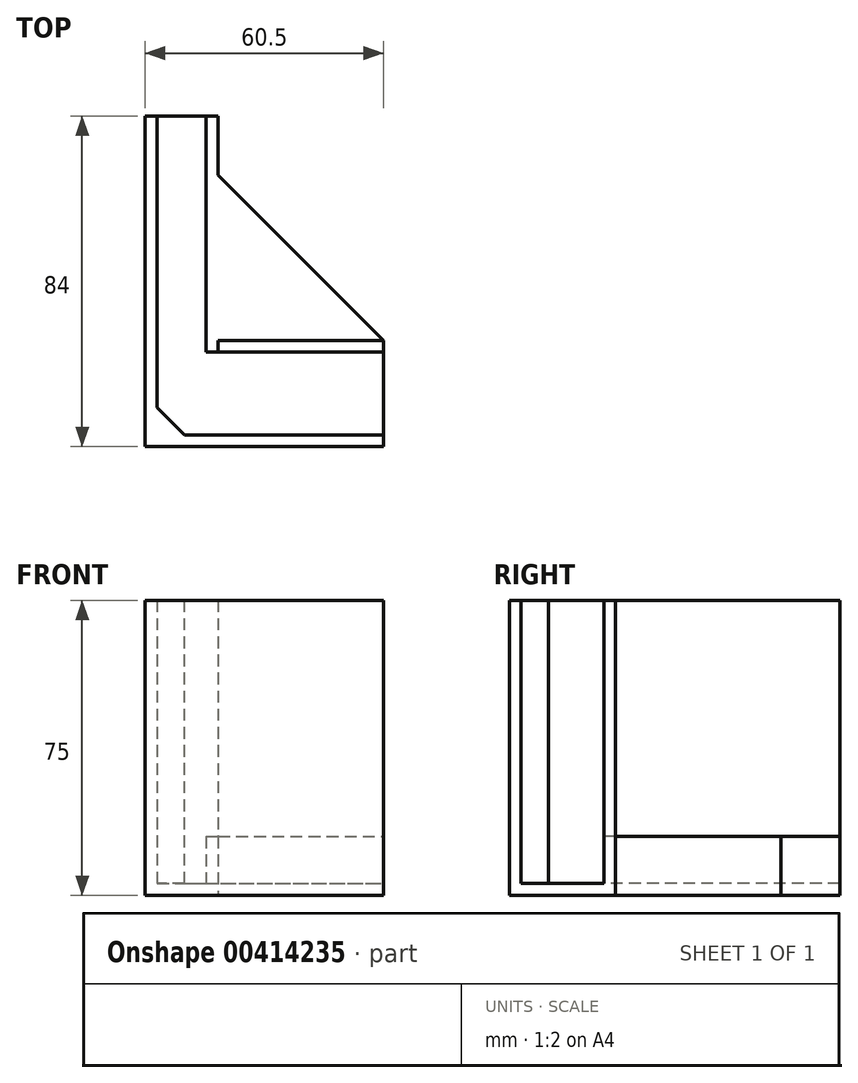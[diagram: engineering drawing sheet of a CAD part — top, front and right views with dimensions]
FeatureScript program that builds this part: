
annotation { "Feature Type Name" : "Feature", "Feature Type Description" : "" }
export const myFeature = defineFeature(function(context is Context, id is Id, definition is map)
    precondition{}
    {
        {
            var Q0;
            Q0=qCreatedBy(makeId("Top.planeOp"),FACE);
            var sketch = newSketch(context, id + "F0", { "sketchPlane" : qUnion([Q0])});
            skLineSegment(sketch, "E0", {"start": v(-12.5, 60) * mm, "end": v(0, 60) * mm});
            skLineSegment(sketch, "E1", {"start": v(0, 60) * mm, "end": v(0, 0) * mm});
            skLineSegment(sketch, "E2", {"start": v(0, 0) * mm, "end": v(45, 0) * mm});
            skLineSegment(sketch, "E3", {"start": v(45, 0) * mm, "end": v(45, -21) * mm});
            skLineSegment(sketch, "E4", {"start": v(-12.5, 60) * mm, "end": v(-12.5, -21) * mm});
            skLineSegment(sketch, "E5", {"start": v(-12.5, -21) * mm, "end": v(45, -21) * mm});
            skLineSegment(sketch, "E6", {"start": v(-12.5, 60) * mm, "end": v(-15.5, 60) * mm});
            skLineSegment(sketch, "E7", {"start": v(-15.5, 60) * mm, "end": v(-15.5, -24) * mm});
            skLineSegment(sketch, "E8", {"start": v(-15.5, -24) * mm, "end": v(45, -24) * mm});
            skLineSegment(sketch, "E9", {"start": v(45, -24) * mm, "end": v(45, -21) * mm});
            skLineSegment(sketch, "E10", {"start": v(0, 60) * mm, "end": v(3, 60) * mm});
            skLineSegment(sketch, "E11", {"start": v(3, 60) * mm, "end": v(3, 3) * mm});
            skLineSegment(sketch, "E12", {"start": v(3, 3) * mm, "end": v(45, 3) * mm});
            skLineSegment(sketch, "E13", {"start": v(45, 3) * mm, "end": v(45, 0) * mm});
            skSolve(sketch);
        }
        {
            var Q0;
            Q0=makeQuery(id+"F0.imprint","IMPRINT",FACE,{"disambiguationData":[TD([[makeQuery(id+"F0.imprint","IMPRINT",EDGE,{"derivedFrom":sQuery(id+"F0.wireOp",EDGE,"E0")}),-1.0]])]});
            extrude(context, id + "F1", {"entities" : qUnion([Q0]), "depth" : 3 * mm});
        }
        {
            var Q0;
            Q0=makeQuery(id+"F0.imprint","IMPRINT",FACE,{"disambiguationData":[TD([[makeQuery(id+"F0.imprint","IMPRINT",EDGE,{"derivedFrom":sQuery(id+"F0.wireOp",EDGE,"E4")}),-1.0]])]});
            extrude(context, id + "F2", {"entities" : qUnion([Q0]), "operationType" : NewBodyOperationType.ADD, "depth" : 75 * mm});
        }
        {
            var Q0;
            Q0=makeQuery(id+"F0.imprint","IMPRINT",FACE,{"disambiguationData":[TD([[makeQuery(id+"F0.imprint","IMPRINT",EDGE,{"derivedFrom":sQuery(id+"F0.wireOp",EDGE,"E1")}),1.0]])]});
            extrude(context, id + "F3", {"entities" : qUnion([Q0]), "operationType" : NewBodyOperationType.ADD, "depth" : 15 * mm});
        }
        {
            var Q0;
            Q0=makeQuery(id+"F2.opExtrude","SWEPT_EDGE",EDGE,{"disambiguationData":[OSD([sQuery(id+"F0.wireOp",EDGE,"E4"),sQuery(id+"F0.wireOp",EDGE,"E5")])]});
            chamfer(context, id + "F4", {"entities" : qUnion([Q0]), "width" : 7 * mm, "tangentPropagation" : true});
        }
        {
            var Q0;
            Q0=makeQuery(id+"F3.opExtrude","CAP_FACE",FACE,{"disambiguationData":[OSD([sQuery(id+"F0.wireOp",EDGE,"E1"),sQuery(id+"F0.wireOp",EDGE,"E2"),sQuery(id+"F0.wireOp",EDGE,"E10"),sQuery(id+"F0.wireOp",EDGE,"E11"),sQuery(id+"F0.wireOp",EDGE,"E12"),sQuery(id+"F0.wireOp",EDGE,"E13")])],"isStart":false});
            var sketch = newSketch(context, id + "F5", { "sketchPlane" : qUnion([Q0])});
            skLineSegment(sketch, "E14", {"start": v(3, 3) * mm, "end": v(3, 0) * mm});
            skLineSegment(sketch, "E15", {"start": v(3, 0) * mm, "end": v(45, 0) * mm});
            skLineSegment(sketch, "E16", {"start": v(45, 0) * mm, "end": v(45, 3) * mm});
            skLineSegment(sketch, "E17", {"start": v(45, 3) * mm, "end": v(3, 3) * mm});
            skSolve(sketch);
        }
        {
            var Q0;
            Q0 = qSketchRegion(id + "F5", true);
            var Q1;
            Q1=makeQuery(id+"F2.opExtrude","CAP_FACE",FACE,{"disambiguationData":[OSD([sQuery(id+"F0.wireOp",EDGE,"E4"),sQuery(id+"F0.wireOp",EDGE,"E5"),sQuery(id+"F0.wireOp",EDGE,"E6"),sQuery(id+"F0.wireOp",EDGE,"E7"),sQuery(id+"F0.wireOp",EDGE,"E8"),sQuery(id+"F0.wireOp",EDGE,"E9")])],"isStart":false});
            extrude(context, id + "F6", {"entities" : qUnion([Q0]), "operationType" : NewBodyOperationType.ADD, "endBound" : BoundingType.UP_TO_SURFACE, "endBoundEntityFace" : qUnion([Q1]), "depth" : 25 * mm});
        }
        {
            var Q0;
            {var subQ0=sQuery(id+"F0.wireOp",EDGE,"E2");var subQ1=sQuery(id+"F0.wireOp",EDGE,"E1");var subQ2=sQuery(id+"F0.wireOp",EDGE,"E5");var subQ3=sQuery(id+"F0.wireOp",EDGE,"E4");Q0=makeQuery(id+"F3.boolean.opBoolean","MERGE",FACE,{"derivedFrom":[makeQuery(id+"F2.boolean.opBoolean","MERGE",FACE,{"derivedFrom":[makeQuery(id+"F1.opExtrude","CAP_FACE",FACE,{"disambiguationData":[OSD([sQuery(id+"F0.wireOp",EDGE,"E0"),subQ1,subQ0,sQuery(id+"F0.wireOp",EDGE,"E3"),subQ3,subQ2])],"isStart":true}),makeQuery(id+"F2.opExtrude","CAP_FACE",FACE,{"disambiguationData":[OSD([subQ3,subQ2,sQuery(id+"F0.wireOp",EDGE,"E6"),sQuery(id+"F0.wireOp",EDGE,"E7"),sQuery(id+"F0.wireOp",EDGE,"E8"),sQuery(id+"F0.wireOp",EDGE,"E9")])],"isStart":true})]}),makeQuery(id+"F3.opExtrude","CAP_FACE",FACE,{"disambiguationData":[OSD([subQ1,subQ0,sQuery(id+"F0.wireOp",EDGE,"E10"),sQuery(id+"F0.wireOp",EDGE,"E11"),sQuery(id+"F0.wireOp",EDGE,"E12"),sQuery(id+"F0.wireOp",EDGE,"E13")])],"isStart":true})]});}
            var sketch = newSketch(context, id + "F7", { "sketchPlane" : qUnion([Q0])});
            skLineSegment(sketch, "E18", {"start": v(45, -3) * mm, "end": v(3, -3) * mm});
            skLineSegment(sketch, "E19", {"start": v(3, -3) * mm, "end": v(3, -45) * mm});
            skLineSegment(sketch, "E20", {"start": v(3, -45) * mm, "end": v(45, -3) * mm});
            skSolve(sketch);
        }
        {
            var Q0;
            Q0 = qSketchRegion(id + "F7", true);
            var Q1;
            Q1=makeQuery(id+"F3.opExtrude","CAP_FACE",FACE,{"disambiguationData":[OSD([sQuery(id+"F0.wireOp",EDGE,"E1"),sQuery(id+"F0.wireOp",EDGE,"E2"),sQuery(id+"F0.wireOp",EDGE,"E10"),sQuery(id+"F0.wireOp",EDGE,"E11"),sQuery(id+"F0.wireOp",EDGE,"E12"),sQuery(id+"F0.wireOp",EDGE,"E13")])],"isStart":false});
            extrude(context, id + "F8", {"entities" : qUnion([Q0]), "operationType" : NewBodyOperationType.ADD, "endBound" : BoundingType.UP_TO_SURFACE, "oppositeDirection" : true, "endBoundEntityFace" : qUnion([Q1]), "depth" : 11.6 * mm});
        }
    });
